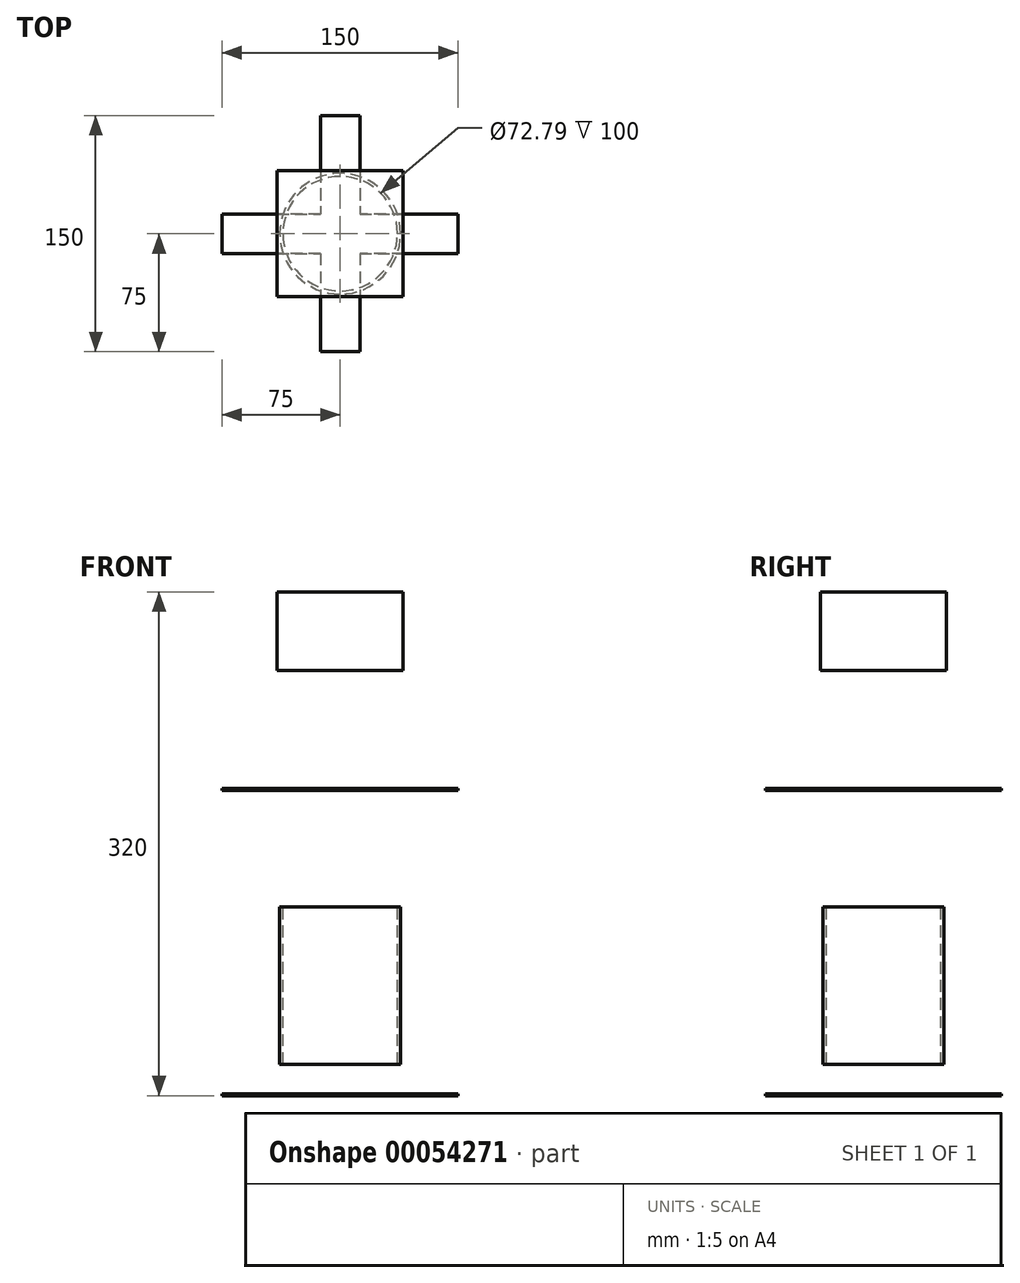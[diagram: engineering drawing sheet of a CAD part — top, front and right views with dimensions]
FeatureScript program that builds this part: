
annotation { "Feature Type Name" : "Feature", "Feature Type Description" : "" }
export const myFeature = defineFeature(function(context is Context, id is Id, definition is map)
    precondition{}
    {
        {
            var Q0;
            Q0=qCreatedBy(makeId("Top.planeOp"),FACE);
            var sketch = newSketch(context, id + "F0", { "sketchPlane" : qUnion([Q0])});
            skCircle(sketch, "E0", {"center": v(0, 0) * mm, "radius": 38.37 * mm});
            skSolve(sketch);
        }
        {
            var Q0;
            Q0=makeQuery(id+"F0.imprint","IMPRINT",FACE,{"disambiguationData":[TD([[makeQuery(id+"F0.imprint","IMPRINT",EDGE,{"derivedFrom":sQuery(id+"F0.wireOp",EDGE,"E0")}),1.0]])]});
            extrude(context, id + "F1", {"entities" : qUnion([Q0]), "oppositeDirection" : true, "depth" : 100 * mm});
        }
        {
            var Q0;
            Q0=makeQuery(id+"F1.opExtrude","CAP_FACE",FACE,{"disambiguationData":[OSD([sQuery(id+"F0.wireOp",EDGE,"E0")])],"isStart":true});
            var sketch = newSketch(context, id + "F2", { "sketchPlane" : qUnion([Q0])});
            skCircle(sketch, "E1", {"center": v(0, 0) * mm, "radius": 36.4 * mm});
            skSolve(sketch);
        }
        {
            var Q0;
            Q0=makeQuery(id+"F2.imprint","IMPRINT",FACE,{"disambiguationData":[TD([[makeQuery(id+"F2.imprint","IMPRINT",EDGE,{"derivedFrom":sQuery(id+"F2.wireOp",EDGE,"E1")}),1.0]])]});
            extrude(context, id + "F3", {"entities" : qUnion([Q0]), "operationType" : NewBodyOperationType.REMOVE, "oppositeDirection" : true, "depth" : 100 * mm});
        }
        {
            var Q0;
            Q0=qCreatedBy(makeId("Top.planeOp"),FACE);
            cPlane(context, id + "F4", {"entities" : qUnion([Q0]), "cplaneType" : CPlaneType.OFFSET, "offset" : 150 * mm, "width" : 150 * mm, "height" : 150 * mm});
        }
        {
            var Q0;
            Q0=qCreatedBy(id+"F4.planeOp",FACE);
            var sketch = newSketch(context, id + "F5", { "sketchPlane" : qUnion([Q0])});
            skLineSegment(sketch, "E2.rect.bottom", {"start": v(40, -40) * mm, "end": v(-40, -40) * mm});
            skLineSegment(sketch, "E2.rect.top", {"start": v(40, 40) * mm, "end": v(-40, 40) * mm});
            skLineSegment(sketch, "E2.rect.left", {"start": v(40, -40) * mm, "end": v(40, 40) * mm});
            skLineSegment(sketch, "E2.rect.right", {"start": v(-40, -40) * mm, "end": v(-40, 40) * mm});
            skPoint(sketch, "E2.rect.middle", {"position": v(0, 0) * mm});
            skSolve(sketch);
        }
        {
            var Q0;
            Q0=makeQuery(id+"F5.imprint","IMPRINT",FACE,{"disambiguationData":[TD([[makeQuery(id+"F5.imprint","IMPRINT",EDGE,{"derivedFrom":sQuery(id+"F5.wireOp",EDGE,"E2.rect.bottom")}),-1.0]])]});
            extrude(context, id + "F6", {"entities" : qUnion([Q0]), "depth" : 50 * mm});
        }
        {
            var Q0;
            Q0=qCreatedBy(makeId("Top.planeOp"),FACE);
            cPlane(context, id + "F7", {"entities" : qUnion([Q0]), "cplaneType" : CPlaneType.OFFSET, "offset" : 150 * mm, "oppositeDirection" : true, "width" : 150 * mm, "height" : 150 * mm});
        }
        {
            var Q0;
            Q0=qCreatedBy(id+"F7.planeOp",FACE);
            var sketch = newSketch(context, id + "F8", { "sketchPlane" : qUnion([Q0])});
            skCircle(sketch, "E3", {"center": v(0, 0) * mm, "radius": 3.03 * mm});
            skSolve(sketch);
        }
        {
            var Q0;
            Q0=sQuery(id+"F8.wireOp",EDGE,"E3");
            extrude(context, id + "F9", {"bodyType" : ToolBodyType.SURFACE, "surfaceEntities" : qUnion([Q0]), "depth" : 300 * mm});
        }
        {
            var Q0;
            Q0=qCreatedBy(makeId("Top.planeOp"),FACE);
            cPlane(context, id + "F10", {"entities" : qUnion([Q0]), "cplaneType" : CPlaneType.OFFSET, "offset" : 75 * mm, "width" : 150 * mm, "height" : 150 * mm});
        }
        {
            var Q0;
            Q0=qCreatedBy(id+"F10.planeOp",FACE);
            var sketch = newSketch(context, id + "F11", { "sketchPlane" : qUnion([Q0])});
            skLineSegment(sketch, "E4.rect.bottom", {"start": v(-75, 12.5) * mm, "end": v(75, 12.5) * mm});
            skLineSegment(sketch, "E4.rect.top", {"start": v(-75, -12.5) * mm, "end": v(75, -12.5) * mm});
            skLineSegment(sketch, "E4.rect.left", {"start": v(-75, 12.5) * mm, "end": v(-75, -12.5) * mm});
            skLineSegment(sketch, "E4.rect.right", {"start": v(75, 12.5) * mm, "end": v(75, -12.5) * mm});
            skPoint(sketch, "E4.rect.middle", {"position": v(0, 0) * mm});
            skLineSegment(sketch, "E5.rect.bottom", {"start": v(-12.5, 75) * mm, "end": v(12.5, 75) * mm});
            skLineSegment(sketch, "E5.rect.top", {"start": v(-12.5, -75) * mm, "end": v(12.5, -75) * mm});
            skLineSegment(sketch, "E5.rect.left", {"start": v(-12.5, 75) * mm, "end": v(-12.5, -75) * mm});
            skLineSegment(sketch, "E5.rect.right", {"start": v(12.5, 75) * mm, "end": v(12.5, -75) * mm});
            skSolve(sketch);
        }
        {
            var Q0;
            Q0 = qSketchRegion(id + "F11", true);
            extrude(context, id + "F12", {"entities" : qUnion([Q0]), "oppositeDirection" : true, "depth" : 1 * mm});
        }
        {
            var Q0;
            Q0=qCreatedBy(id+"F7.planeOp",FACE);
            cPlane(context, id + "F13", {"entities" : qUnion([Q0]), "cplaneType" : CPlaneType.OFFSET, "offset" : 30 * mm, "width" : 150 * mm, "height" : 150 * mm});
        }
        {
            var Q0;
            Q0=qCreatedBy(id+"F13.planeOp",FACE);
            var sketch = newSketch(context, id + "F14", { "sketchPlane" : qUnion([Q0])});
            skLineSegment(sketch, "E6.rect.bottom", {"start": v(75, 12.5) * mm, "end": v(-75, 12.5) * mm});
            skLineSegment(sketch, "E6.rect.top", {"start": v(75, -12.5) * mm, "end": v(-75, -12.5) * mm});
            skLineSegment(sketch, "E6.rect.left", {"start": v(75, 12.5) * mm, "end": v(75, -12.5) * mm});
            skLineSegment(sketch, "E6.rect.right", {"start": v(-75, 12.5) * mm, "end": v(-75, -12.5) * mm});
            skPoint(sketch, "E6.rect.middle", {"position": v(0, 0) * mm});
            skLineSegment(sketch, "E7.rect.bottom", {"start": v(12.5, 75) * mm, "end": v(-12.5, 75) * mm});
            skLineSegment(sketch, "E7.rect.top", {"start": v(12.5, -75) * mm, "end": v(-12.5, -75) * mm});
            skLineSegment(sketch, "E7.rect.left", {"start": v(12.5, 75) * mm, "end": v(12.5, -75) * mm});
            skLineSegment(sketch, "E7.rect.right", {"start": v(-12.5, 75) * mm, "end": v(-12.5, -75) * mm});
            skSolve(sketch);
        }
        {
            var Q0;
            Q0 = qSketchRegion(id + "F14", true);
            extrude(context, id + "F15", {"entities" : qUnion([Q0]), "operationType" : NewBodyOperationType.ADD, "depth" : 1 * mm});
        }
    });
